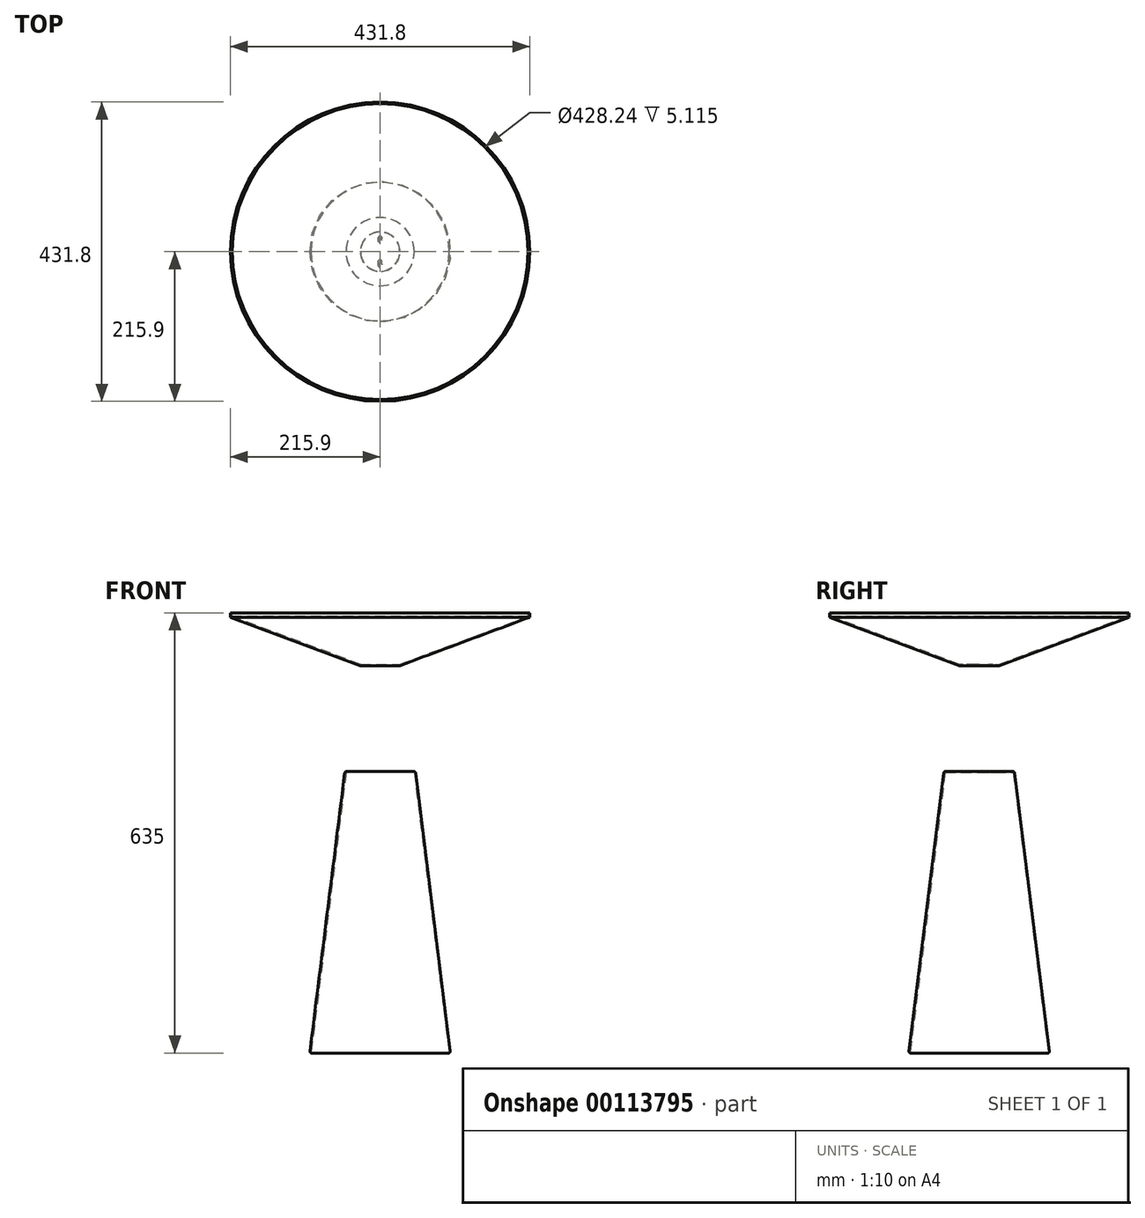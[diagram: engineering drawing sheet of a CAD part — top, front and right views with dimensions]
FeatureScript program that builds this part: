
annotation { "Feature Type Name" : "Feature", "Feature Type Description" : "" }
export const myFeature = defineFeature(function(context is Context, id is Id, definition is map)
    precondition{}
    {
        {
            var Q0;
            Q0=qCreatedBy(makeId("Front.planeOp"),FACE);
            var sketch = newSketch(context, id + "F0", { "sketchPlane" : qUnion([Q0])});
            skLineSegment(sketch, "E0.bottom", {"start": v(215.9, -317.5) * mm, "end": v(0, -317.5) * mm, "construction": true});
            skLineSegment(sketch, "E0.top", {"start": v(215.9, 317.5) * mm, "end": v(0, 317.5) * mm});
            skLineSegment(sketch, "E0.left", {"start": v(215.9, -317.5) * mm, "end": v(215.9, 317.5) * mm, "construction": true});
            skPoint(sketch, "E0.middle", {"position": v(0, 0) * mm});
            skLineSegment(sketch, "E1.0", {"start": v(28.57, 241.3) * mm, "end": v(25.4, 241.3) * mm});
            skLineSegment(sketch, "E2", {"start": v(0, -317.5) * mm, "end": v(101.6, -317.5) * mm});
            skLineSegment(sketch, "E3", {"start": v(38.1, 88.9) * mm, "end": v(50.8, 88.9) * mm});
            skLineSegment(sketch, "E4", {"start": v(50.8, 88.9) * mm, "end": v(101.6, -317.5) * mm});
            skLineSegment(sketch, "E5", {"start": v(28.57, 241.3) * mm, "end": v(215.9, 311.15) * mm});
            skPoint(sketch, "E6.orphan", {"position": v(215.9, 241.3) * mm});
            skPoint(sketch, "E7.orphan", {"position": v(-215.9, 241.3) * mm});
            skPoint(sketch, "E8.orphan", {"position": v(-215.9, 317.5) * mm});
            skPoint(sketch, "E9.orphan", {"position": v(-215.9, -317.5) * mm});
            skLineSegment(sketch, "E10", {"start": v(215.9, 311.15) * mm, "end": v(215.9, 317.5) * mm});
            skLineSegment(sketch, "E11", {"start": v(0, 241.3) * mm, "end": v(25.4, 241.3) * mm});
            skLineSegment(sketch, "E12", {"start": v(0, 88.9) * mm, "end": v(38.1, 88.9) * mm});
            skLineSegment(sketch, "E13", {"start": v(0, 317.5) * mm, "end": v(0, 241.3) * mm});
            skLineSegment(sketch, "E14", {"start": v(0, 88.9) * mm, "end": v(0, -317.5) * mm});
            skSolve(sketch);
        }
        {
            var Q0;
            Q0=makeQuery(id+"F0.imprint","IMPRINT",FACE,{"disambiguationData":[TD([[makeQuery(id+"F0.imprint","IMPRINT",EDGE,{"derivedFrom":sQuery(id+"F0.wireOp",EDGE,"E0.top")}),1.0]])]});
            var Q1;
            Q1=makeQuery(id+"F0.imprint","IMPRINT",FACE,{"disambiguationData":[TD([[makeQuery(id+"F0.imprint","IMPRINT",EDGE,{"derivedFrom":sQuery(id+"F0.wireOp",EDGE,"E2")}),1.0]])]});
            var Q2;
            Q2=sQuery(id+"F0.wireOp",EDGE,"E13");
            revolve(context, id + "F1", {"entities" : qUnion([Q0, Q1]), "axis" : qUnion([Q2]), "revolveType" : RevolveType.FULL});
        }
        {
            var Q0;
            Q0=makeQuery(id+"F1.opRevolve","SWEPT_FACE",FACE,{"disambiguationData":[OSD([sQuery(id+"F0.wireOp",EDGE,"E2")])]});
            shell(context, id + "F2", {"entities" : qUnion([Q0]), "thickness" : 1.78 * mm});
        }
        {
            var Q0;
            Q0=makeQuery(id+"F1.opRevolve","SWEPT_FACE",FACE,{"disambiguationData":[OSD([sQuery(id+"F0.wireOp",EDGE,"E0.top")])]});
            shell(context, id + "F3", {"entities" : qUnion([Q0]), "thickness" : 1.78 * mm});
        }
        {
            var Q0;
            Q0=makeQuery(id+"F1.opRevolve","SWEPT_FACE",FACE,{"disambiguationData":[OSD([sQuery(id+"F0.wireOp",EDGE,"E0.top")])]});
            var sketch = newSketch(context, id + "F4", { "sketchPlane" : qUnion([Q0])});
            skCircle(sketch, "E15.0", {"center": v(0, 0) * mm, "radius": 213.33 * mm});
            skSolve(sketch);
        }
        {
            var Q0;
            Q0 = qSketchRegion(id + "F4", true);
            extrude(context, id + "F5", {"entities" : qUnion([Q0]), "oppositeDirection" : true, "depth" : 6.35 * mm});
        }
        {
            var Q0;
            Q0=makeQuery(id+"F1.opRevolve","SWEPT_EDGE",EDGE,{"disambiguationData":[OSD([sQuery(id+"F0.wireOp",EDGE,"E3"),sQuery(id+"F0.wireOp",EDGE,"E4")])]});
            var Q1;
            Q1=makeQuery(id+"F1.opRevolve","SWEPT_EDGE",EDGE,{"disambiguationData":[OSD([sQuery(id+"F0.wireOp",EDGE,"E2"),sQuery(id+"F0.wireOp",EDGE,"E4")])]});
            fillet(context, id + "F6", {"entities" : qUnion([Q0, Q1]), "radius" : 3.17 * mm, "tangentPropagation" : true, "allowEdgeOverflow" : false});
        }
        {
            var Q0;
            Q0=makeQuery(id+"F1.opRevolve","SWEPT_FACE",FACE,{"disambiguationData":[OSD([sQuery(id+"F0.wireOp",EDGE,"E1.0"),sQuery(id+"F0.wireOp",EDGE,"E11")])]});
            var sketch = newSketch(context, id + "F7", { "sketchPlane" : qUnion([Q0])});
            skCircle(sketch, "E16", {"center": v(-0.22, -0.77) * mm, "radius": 15.87 * mm, "construction": true});
            skPoint(sketch, "E17", {"position": v(-0.22, 15.1) * mm});
            skPoint(sketch, "E18", {"position": v(-0.22, -16.64) * mm});
            skSolve(sketch);
        }
        {
            var Q0;
            Q0=sQuery(id+"F7.wireOp",VERTEX,"E17");
            var Q1;
            Q1=sQuery(id+"F7.wireOp",VERTEX,"E18");
            var Q2;
            Q2=makeQuery(id+"F1.opRevolve","SWEPT_BODY",BODY,{"disambiguationData":[OSD([sQuery(id+"F0.wireOp",EDGE,"E0.top"),sQuery(id+"F0.wireOp",EDGE,"E1.0"),sQuery(id+"F0.wireOp",EDGE,"E5"),sQuery(id+"F0.wireOp",EDGE,"E10"),sQuery(id+"F0.wireOp",EDGE,"E11"),sQuery(id+"F0.wireOp",EDGE,"E13")])]});
            hole(context, id + "F8", {"style" : HoleStyle.SIMPLE, "endStyle" : HoleEndStyle.BLIND, "holeDiameter" : 6.1 * mm, "holeDepth" : 5.08 * mm, "locations" : qUnion([Q0, Q1]), "scope" : qUnion([Q2])});
        }
        {
            var Q0;
            Q0=makeQuery(id+"F1.opRevolve","SWEPT_FACE",FACE,{"disambiguationData":[OSD([sQuery(id+"F0.wireOp",EDGE,"E3"),sQuery(id+"F0.wireOp",EDGE,"E12")])]});
            var sketch = newSketch(context, id + "F9", { "sketchPlane" : qUnion([Q0])});
            skCircle(sketch, "E19", {"center": v(-0.07, 0.07) * mm, "radius": 19.05 * mm, "construction": true});
            skPoint(sketch, "E20", {"position": v(-0.07, 19.12) * mm});
            skPoint(sketch, "E21", {"position": v(-0.07, -18.98) * mm});
            skSolve(sketch);
        }
        {
            var Q0;
            Q0=sQuery(id+"F9.wireOp",VERTEX,"E21");
            var Q1;
            Q1=sQuery(id+"F9.wireOp",VERTEX,"E20");
            var Q2;
            Q2=makeQuery(id+"F1.opRevolve","SWEPT_BODY",BODY,{"disambiguationData":[OSD([sQuery(id+"F0.wireOp",EDGE,"E2"),sQuery(id+"F0.wireOp",EDGE,"E3"),sQuery(id+"F0.wireOp",EDGE,"E4"),sQuery(id+"F0.wireOp",EDGE,"E12"),sQuery(id+"F0.wireOp",EDGE,"E14")])]});
            hole(context, id + "F10", {"style" : HoleStyle.SIMPLE, "endStyle" : HoleEndStyle.BLIND, "holeDiameter" : 6.1 * mm, "holeDepth" : 5.08 * mm, "locations" : qUnion([Q0, Q1]), "scope" : qUnion([Q2])});
        }
    });
